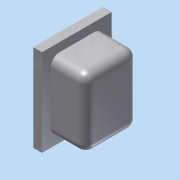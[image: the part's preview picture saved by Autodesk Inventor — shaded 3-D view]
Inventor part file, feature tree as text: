
AUTODESK INVENTOR PART (.ipt)
format: ipt  version: 2015 (Build 190159000, 159)  size: 111,104 bytes
history: native  units: in
note: dims shown in document units (in); Inventor stores cm internally (conversion verified against a paired STEP export)
features: extrude x2, sketch x2, fillet x1, projected_geometry x1
ambient origin geometry x8: Origin, YZ Plane, XZ Plane, XY Plane, X Axis, Y Axis, Z Axis, Center Point
bodies: Solid1 (feature_tree)
feature tree (6):
  extrude  "Extrusion1"  Depth=0.373in
  extrude  "Extrusion2"  Depth=0.0625in
  fillet  "Fillet1"  Radius=0.0625in
  sketch  "Sketch1"  dims[d0=0.498in d1=0.373in]
  sketch  "Sketch2"  dims[d2=0.25in d3=0.0in d4=0.0625in d5=0.0625in d6=0.0in d7=0.0625in]
  projected_geometry  "Projected Loop1"
